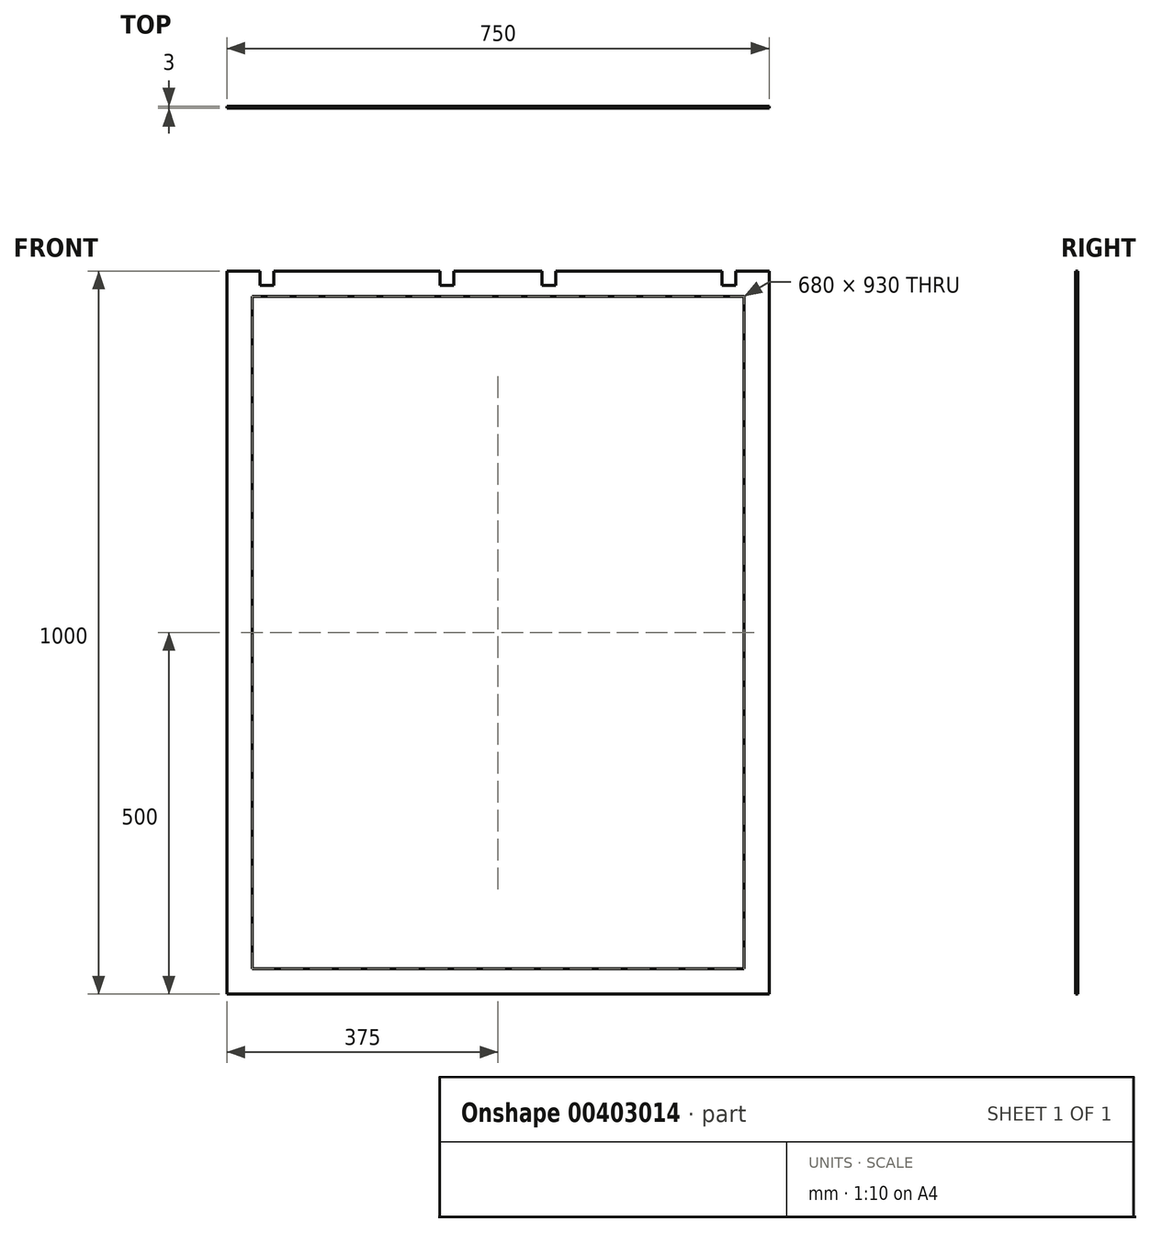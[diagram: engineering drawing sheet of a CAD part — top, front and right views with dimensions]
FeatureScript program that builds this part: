
annotation { "Feature Type Name" : "Feature", "Feature Type Description" : "" }
export const myFeature = defineFeature(function(context is Context, id is Id, definition is map)
    precondition{}
    {
        {
            var Q0;
            Q0=qCreatedBy(makeId("Front.planeOp"),FACE);
            var sketch = newSketch(context, id + "F0", { "sketchPlane" : qUnion([Q0])});
            skLineSegment(sketch, "E0.bottom", {"start": v(0, 0) * mm, "end": v(750, 0) * mm});
            skLineSegment(sketch, "E0.top", {"start": v(0, 1000) * mm, "end": v(46, 1000) * mm});
            skLineSegment(sketch, "E0.left", {"start": v(0, 0) * mm, "end": v(0, 1000) * mm});
            skLineSegment(sketch, "E0.right", {"start": v(750, 0) * mm, "end": v(750, 1000) * mm});
            skLineSegment(sketch, "E1.top", {"start": v(46, 980) * mm, "end": v(65, 980) * mm});
            skLineSegment(sketch, "E1.left", {"start": v(46, 1000) * mm, "end": v(46, 980) * mm});
            skLineSegment(sketch, "E1.right", {"start": v(65, 1000) * mm, "end": v(65, 980) * mm});
            skLineSegment(sketch, "E2.top", {"start": v(685, 980) * mm, "end": v(704, 980) * mm});
            skLineSegment(sketch, "E2.left", {"start": v(685, 1000) * mm, "end": v(685, 980) * mm});
            skLineSegment(sketch, "E2.right", {"start": v(704, 1000) * mm, "end": v(704, 980) * mm});
            skLineSegment(sketch, "E3.trimOffspring", {"start": v(65, 1000) * mm, "end": v(295, 1000) * mm});
            skLineSegment(sketch, "E4.trimOffspring", {"start": v(704, 1000) * mm, "end": v(750, 1000) * mm});
            skLineSegment(sketch, "E5.top", {"start": v(295, 980) * mm, "end": v(314, 980) * mm});
            skLineSegment(sketch, "E5.left", {"start": v(295, 1000) * mm, "end": v(295, 980) * mm});
            skLineSegment(sketch, "E5.right", {"start": v(314, 1000) * mm, "end": v(314, 980) * mm});
            skLineSegment(sketch, "E6.trimOffspring", {"start": v(314, 1000) * mm, "end": v(436, 1000) * mm});
            skLineSegment(sketch, "E7.top", {"start": v(436, 980) * mm, "end": v(455, 980) * mm});
            skLineSegment(sketch, "E7.left", {"start": v(436, 1000) * mm, "end": v(436, 980) * mm});
            skLineSegment(sketch, "E7.right", {"start": v(455, 1000) * mm, "end": v(455, 980) * mm});
            skLineSegment(sketch, "E8.trimOffspring", {"start": v(455, 1000) * mm, "end": v(685, 1000) * mm});
            skLineSegment(sketch, "E9.bottom", {"start": v(35, 965) * mm, "end": v(715, 965) * mm});
            skLineSegment(sketch, "E9.top", {"start": v(35, 35) * mm, "end": v(715, 35) * mm});
            skLineSegment(sketch, "E9.left", {"start": v(35, 965) * mm, "end": v(35, 35) * mm});
            skLineSegment(sketch, "E9.right", {"start": v(715, 965) * mm, "end": v(715, 35) * mm});
            skSolve(sketch);
        }
        {
            var Q0;
            Q0=makeQuery(id+"F0.imprint","IMPRINT",FACE,{"disambiguationData":[TD([[makeQuery(id+"F0.imprint","IMPRINT",EDGE,{"derivedFrom":sQuery(id+"F0.wireOp",EDGE,"E0.bottom")}),1.0]])]});
            extrude(context, id + "F1", {"entities" : qUnion([Q0]), "depth" : 3 * mm});
        }
    });
